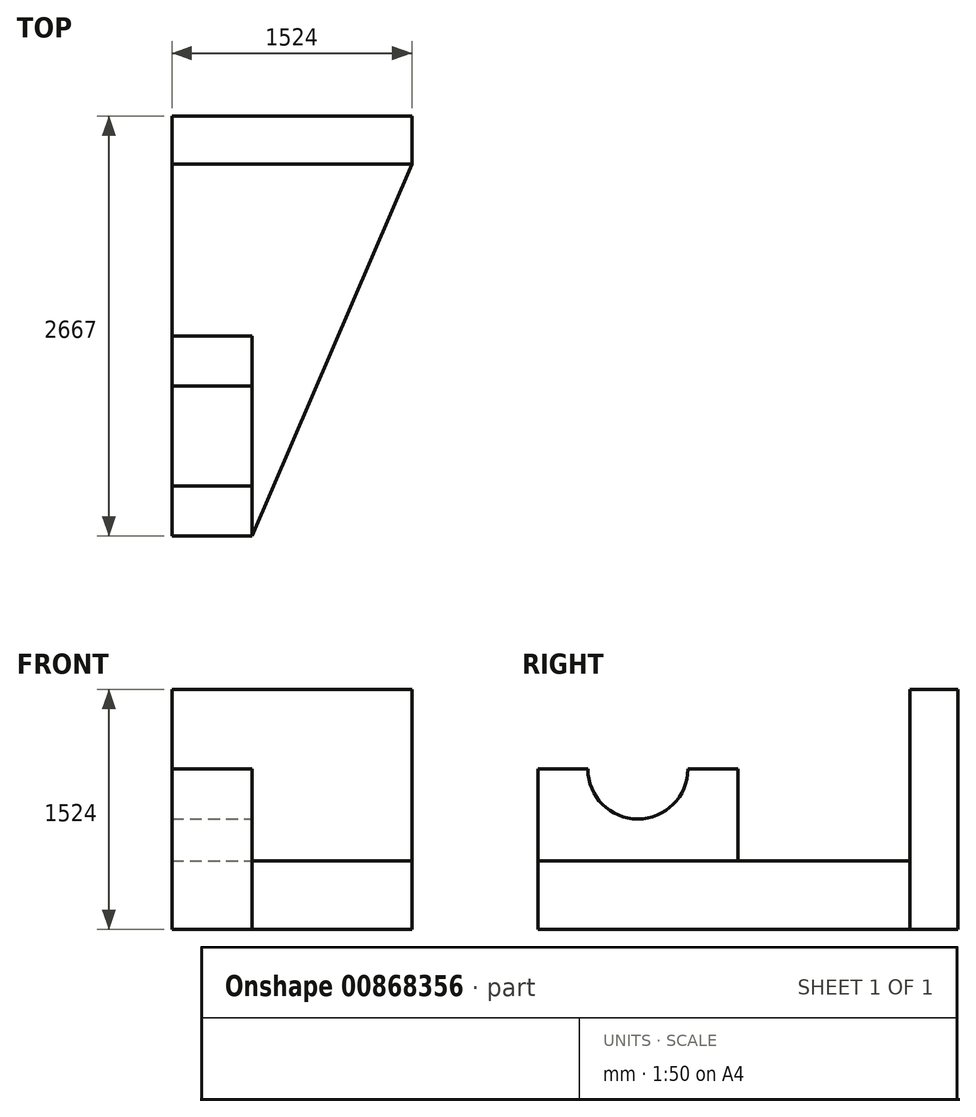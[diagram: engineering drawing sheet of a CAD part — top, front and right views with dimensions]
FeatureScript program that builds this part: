
annotation { "Feature Type Name" : "Feature", "Feature Type Description" : "" }
export const myFeature = defineFeature(function(context is Context, id is Id, definition is map)
    precondition{}
    {
        {
            var Q0;
            Q0=qCreatedBy(makeId("Front.planeOp"),FACE);
            var sketch = newSketch(context, id + "F0", { "sketchPlane" : qUnion([Q0])});
            skLineSegment(sketch, "E0.bottom", {"start": v(0, 0) * mm, "end": v(-1524, 0) * mm});
            skLineSegment(sketch, "E0.top", {"start": v(0, 1524) * mm, "end": v(-1524, 1524) * mm});
            skLineSegment(sketch, "E0.left", {"start": v(0, 0) * mm, "end": v(0, 1524) * mm});
            skLineSegment(sketch, "E0.right", {"start": v(-1524, 0) * mm, "end": v(-1524, 1524) * mm});
            skSolve(sketch);
        }
        {
            var Q0;
            Q0 = qSketchRegion(id + "F0", true);
            extrude(context, id + "F1", {"entities" : qUnion([Q0]), "depth" : 304.8 * mm, "offsetDistance" : 25.4 * mm});
        }
        {
            var Q0;
            Q0=makeQuery(id+"F1.opExtrude","CAP_FACE",FACE,{"disambiguationData":[OSD([sQuery(id+"F0.wireOp",EDGE,"E0.bottom"),sQuery(id+"F0.wireOp",EDGE,"E0.top"),sQuery(id+"F0.wireOp",EDGE,"E0.left"),sQuery(id+"F0.wireOp",EDGE,"E0.right")])],"isStart":false});
            var sketch = newSketch(context, id + "F2", { "sketchPlane" : qUnion([Q0])});
            skLineSegment(sketch, "E1.bottom", {"start": v(-1524, 0) * mm, "end": v(0, 0) * mm});
            skLineSegment(sketch, "E1.top", {"start": v(-1524, 434.05) * mm, "end": v(0, 434.05) * mm});
            skLineSegment(sketch, "E1.left", {"start": v(-1524, 0) * mm, "end": v(-1524, 434.05) * mm});
            skLineSegment(sketch, "E1.right", {"start": v(0, 0) * mm, "end": v(0, 434.05) * mm});
            skSolve(sketch);
        }
        {
            var Q0;
            Q0=makeQuery(id+"F2.imprint","IMPRINT",FACE,{"disambiguationData":[TD([[makeQuery(id+"F2.imprint","IMPRINT",EDGE,{"derivedFrom":sQuery(id+"F2.wireOp",EDGE,"E1.bottom")}),-1.0]])]});
            extrude(context, id + "F3", {"entities" : qUnion([Q0]), "operationType" : NewBodyOperationType.ADD, "depth" : 2362.2 * mm, "offsetDistance" : 25.4 * mm});
        }
        {
            var Q0;
            Q0=makeQuery(id+"F3.opExtrude","SWEPT_FACE",FACE,{"disambiguationData":[OSD([sQuery(id+"F2.wireOp",EDGE,"E1.top")])]});
            var sketch = newSketch(context, id + "F4", { "sketchPlane" : qUnion([Q0])});
            skLineSegment(sketch, "E2.bottom", {"start": v(-1524, -2667) * mm, "end": v(-1016, -2667) * mm});
            skLineSegment(sketch, "E2.top", {"start": v(-1524, -1397) * mm, "end": v(-1016, -1397) * mm});
            skLineSegment(sketch, "E2.left", {"start": v(-1524, -2667) * mm, "end": v(-1524, -1397) * mm});
            skLineSegment(sketch, "E2.right", {"start": v(-1016, -2667) * mm, "end": v(-1016, -1397) * mm});
            skSolve(sketch);
        }
        {
            var Q0;
            Q0=makeQuery(id+"F4.imprint","IMPRINT",FACE,{"disambiguationData":[TD([[makeQuery(id+"F4.imprint","IMPRINT",EDGE,{"derivedFrom":sQuery(id+"F4.wireOp",EDGE,"E2.bottom")}),1.0]])]});
            extrude(context, id + "F5", {"entities" : qUnion([Q0]), "operationType" : NewBodyOperationType.ADD, "depth" : 584.2 * mm, "offsetDistance" : 25.4 * mm});
        }
        {
            var Q0;
            Q0=makeQuery(id+"F5.opExtrude","SWEPT_FACE",FACE,{"disambiguationData":[OSD([sQuery(id+"F4.wireOp",EDGE,"E2.right")])]});
            var sketch = newSketch(context, id + "F6", { "sketchPlane" : qUnion([Q0])});
            skCircle(sketch, "E3", {"center": v(-2032, 1018.25) * mm, "radius": 634.68 * mm});
            skSolve(sketch);
        }
        {
            var Q0;
            {var subQ0=sQuery(id+"F6.wireOp",EDGE,"E3");var subQ1=makeQuery(id+"F5.opExtrude","CAP_EDGE",EDGE,{"disambiguationData":[OSD([sQuery(id+"F4.wireOp",EDGE,"E2.right")])],"isStart":true});var subQ2=makeQuery(id+"F6.imprint","INTERSECT",VERTEX,{"disambiguationData":[OD(0.0)],"derivedFrom":[subQ1,subQ0]});Q0=makeQuery(id+"F6.imprint","IMPRINT",FACE,{"disambiguationData":[TD([[makeQuery(id+"F6.imprint","IMPRINT",EDGE,{"disambiguationData":[TD([[subQ2,-1.0]])],"derivedFrom":subQ0}),1.0]])]});}
            var Q1;
            {var subQ0=sQuery(id+"F6.wireOp",EDGE,"E3");var subQ1=makeQuery(id+"F5.opExtrude","CAP_EDGE",EDGE,{"disambiguationData":[OSD([sQuery(id+"F4.wireOp",EDGE,"E2.right")])],"isStart":false});var subQ2=makeQuery(id+"F6.imprint","INTERSECT",VERTEX,{"disambiguationData":[OD(0.0)],"derivedFrom":[subQ1,subQ0]});Q1=makeQuery(id+"F6.imprint","IMPRINT",FACE,{"disambiguationData":[TD([[makeQuery(id+"F6.imprint","IMPRINT",EDGE,{"disambiguationData":[TD([[subQ2,1.0]])],"derivedFrom":subQ0}),1.0]])]});}
            extrude(context, id + "F7", {"entities" : qUnion([Q0, Q1]), "operationType" : NewBodyOperationType.ADD, "oppositeDirection" : true, "depth" : 508 * mm, "offsetDistance" : 25.4 * mm});
        }
        {
            var Q0;
            {var subQ0=sQuery(id+"F6.wireOp",EDGE,"E3");var subQ1=sQuery(id+"F4.wireOp",EDGE,"E2.right");var subQ2=makeQuery(id+"F5.opExtrude","CAP_EDGE",EDGE,{"disambiguationData":[OSD([subQ1])],"isStart":false});var subQ3=makeQuery(id+"F6.imprint","INTERSECT",VERTEX,{"disambiguationData":[OD(0.0)],"derivedFrom":[subQ2,subQ0]});Q0=makeQuery(id+"F7.boolean.opBoolean","MERGE",FACE,{"derivedFrom":[makeQuery(id+"F5.opExtrude","SWEPT_FACE",FACE,{"disambiguationData":[OSD([subQ1])]}),makeQuery(id+"F7.opExtrude","CAP_FACE",FACE,{"disambiguationData":[OSD([subQ1,subQ0]),TDD([makeQuery(id+"F6.imprint","IMPRINT",EDGE,{"disambiguationData":[TD([[subQ3,1.0]])],"derivedFrom":subQ0}),makeQuery(id+"F6.imprint","IMPRINT",EDGE,{"disambiguationData":[TD([[subQ3,-1.0]])],"derivedFrom":subQ2})])],"isStart":true})]});}
            var sketch = newSketch(context, id + "F8", { "sketchPlane" : qUnion([Q0])});
            skLineSegment(sketch, "E4", {"start": v(-2667, 434.05) * mm, "end": v(-1397, 434.05) * mm});
            skLineSegment(sketch, "E5", {"start": v(-1397, 434.05) * mm, "end": v(-2032, 434.05) * mm});
            skLineSegment(sketch, "E6", {"start": v(-2032, 434.05) * mm, "end": v(-2032, 1652.93) * mm});
            skLineSegment(sketch, "E7", {"start": v(-2032, 1652.93) * mm, "end": v(-2666.68, 1018.25) * mm});
            skLineSegment(sketch, "E8", {"start": v(-2666.68, 1018.25) * mm, "end": v(-1397, 1018.25) * mm});
            skLineSegment(sketch, "E9", {"start": v(-1397, 1018.25) * mm, "end": v(-2032, 1652.93) * mm});
            skCircle(sketch, "E10", {"center": v(-2031.84, 1018.25) * mm, "radius": 317.5 * mm});
            skSolve(sketch);
        }
        {
            var Q0;
            {var subQ0=sQuery(id+"F8.wireOp",EDGE,"E8");var subQ1=sQuery(id+"F8.wireOp",EDGE,"E6");var subQ2=makeQuery(id+"F8.imprint","INTERSECT",VERTEX,{"derivedFrom":[subQ1,subQ0]});Q0=makeQuery(id+"F8.imprint","IMPRINT",FACE,{"disambiguationData":[TD([[makeQuery(id+"F8.imprint","IMPRINT",EDGE,{"disambiguationData":[TD([[subQ2,-1.0]])],"derivedFrom":subQ1}),1.0]])]});}
            var Q1;
            {var subQ0=sQuery(id+"F8.wireOp",EDGE,"E8");var subQ1=sQuery(id+"F8.wireOp",EDGE,"E6");var subQ2=makeQuery(id+"F8.imprint","INTERSECT",VERTEX,{"derivedFrom":[subQ1,subQ0]});Q1=makeQuery(id+"F8.imprint","IMPRINT",FACE,{"disambiguationData":[TD([[makeQuery(id+"F8.imprint","IMPRINT",EDGE,{"disambiguationData":[TD([[subQ2,-1.0]])],"derivedFrom":subQ1}),-1.0]])]});}
            var Q2;
            {var subQ0=sQuery(id+"F8.wireOp",EDGE,"E10");var subQ1=sQuery(id+"F8.wireOp",EDGE,"E6");var subQ2=makeQuery(id+"F8.imprint","INTERSECT",VERTEX,{"disambiguationData":[OD(0.0)],"derivedFrom":[subQ1,subQ0]});Q2=makeQuery(id+"F8.imprint","IMPRINT",FACE,{"disambiguationData":[TD([[makeQuery(id+"F8.imprint","IMPRINT",EDGE,{"disambiguationData":[TD([[subQ2,-1.0]])],"derivedFrom":subQ1}),1.0]])]});}
            var Q3;
            {var subQ0=sQuery(id+"F8.wireOp",EDGE,"E10");var subQ1=sQuery(id+"F8.wireOp",EDGE,"E6");var subQ2=makeQuery(id+"F8.imprint","INTERSECT",VERTEX,{"disambiguationData":[OD(0.0)],"derivedFrom":[subQ1,subQ0]});Q3=makeQuery(id+"F8.imprint","IMPRINT",FACE,{"disambiguationData":[TD([[makeQuery(id+"F8.imprint","IMPRINT",EDGE,{"disambiguationData":[TD([[subQ2,-1.0]])],"derivedFrom":subQ1}),-1.0]])]});}
            extrude(context, id + "F9", {"entities" : qUnion([Q0, Q1, Q2, Q3]), "operationType" : NewBodyOperationType.REMOVE, "oppositeDirection" : true, "depth" : 2413 * mm, "offsetDistance" : 25.4 * mm});
        }
        {
            var Q0;
            Q0=makeQuery(id+"F3.opExtrude","SWEPT_FACE",FACE,{"disambiguationData":[OSD([sQuery(id+"F2.wireOp",EDGE,"E1.top")])]});
            var sketch = newSketch(context, id + "F10", { "sketchPlane" : qUnion([Q0])});
            skLineSegment(sketch, "E11", {"start": v(-1016, -2667) * mm, "end": v(0, -304.8) * mm});
            skSolve(sketch);
        }
        {
            var Q0;
            Q0=makeQuery(id+"F10.imprint","IMPRINT",FACE,{"disambiguationData":[TD([[makeQuery(id+"F10.imprint","IMPRINT",EDGE,{"derivedFrom":sQuery(id+"F10.wireOp",EDGE,"E11")}),-1.0]])]});
            extrude(context, id + "F11", {"entities" : qUnion([Q0]), "operationType" : NewBodyOperationType.REMOVE, "oppositeDirection" : true, "depth" : 1445.26 * mm, "offsetDistance" : 25.4 * mm});
        }
    });
